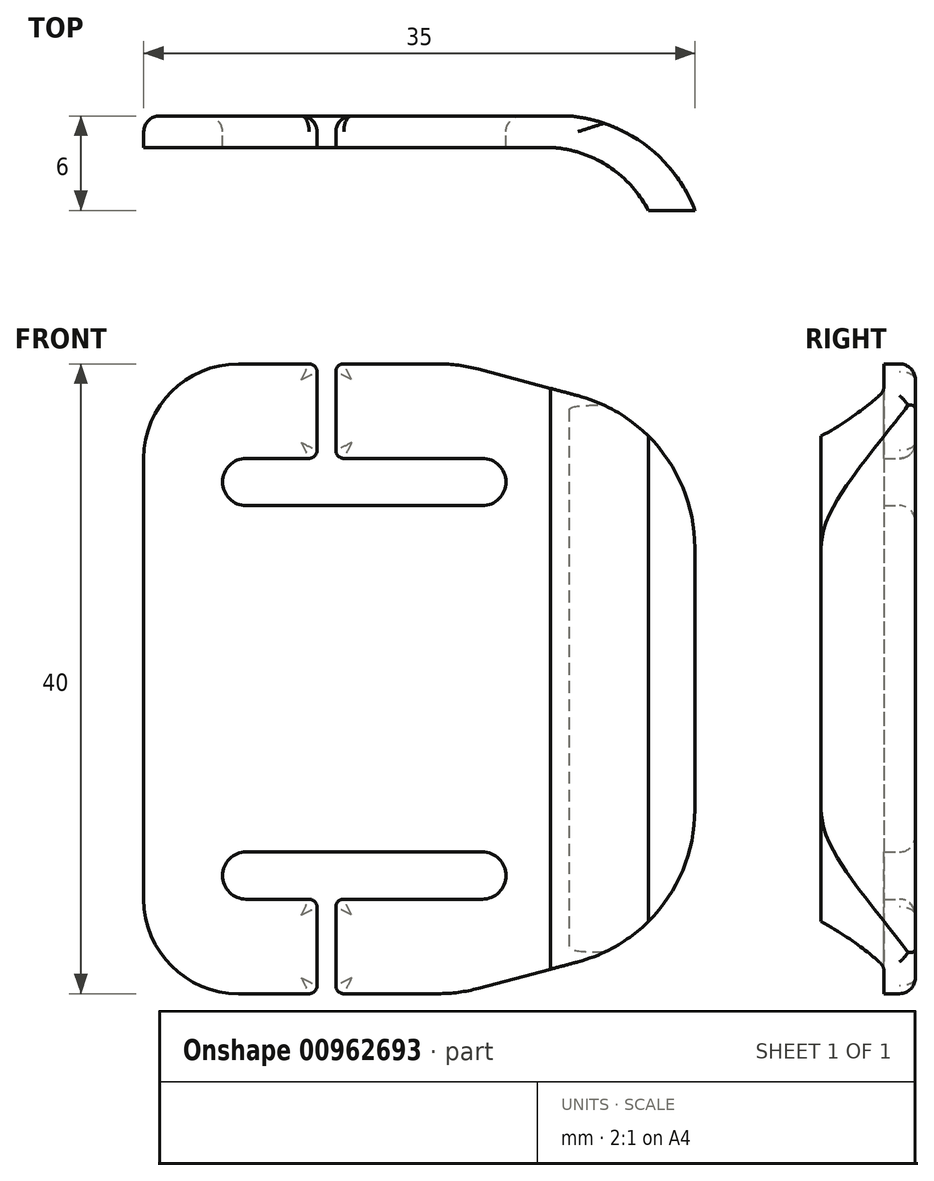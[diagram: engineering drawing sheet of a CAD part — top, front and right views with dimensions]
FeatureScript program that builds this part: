
annotation { "Feature Type Name" : "Feature", "Feature Type Description" : "" }
export const myFeature = defineFeature(function(context is Context, id is Id, definition is map)
    precondition{}
    {
        {
            var Q0;
            Q0=qCreatedBy(makeId("Front.planeOp"),FACE);
            var sketch = newSketch(context, id + "F0", { "sketchPlane" : qUnion([Q0])});
            skLineSegment(sketch, "E0.bottom", {"start": v(1, -20) * mm, "end": v(5.5, -20) * mm});
            skLineSegment(sketch, "E0.top", {"start": v(1, 20) * mm, "end": v(5.5, 20) * mm});
            skLineSegment(sketch, "E0.left", {"start": v(-5, -14) * mm, "end": v(-5, 14) * mm});
            skLineSegment(sketch, "E0.right", {"start": v(30, -8.32) * mm, "end": v(30, 8.32) * mm});
            skLineSegment(sketch, "E1.bottom", {"start": v(1.5, 14) * mm, "end": v(5.5, 14) * mm});
            skLineSegment(sketch, "E1.top", {"start": v(1.5, 11) * mm, "end": v(16.5, 11) * mm});
            skLineSegment(sketch, "E1.left", {"start": v(0, 12.5) * mm, "end": v(0, 12.5) * mm});
            skLineSegment(sketch, "E1.right", {"start": v(18, 12.5) * mm, "end": v(18, 12.5) * mm});
            skLineSegment(sketch, "E2.bottom", {"start": v(1.5, -11) * mm, "end": v(16.5, -11) * mm});
            skLineSegment(sketch, "E2.top", {"start": v(1.5, -14) * mm, "end": v(5.5, -14) * mm});
            skLineSegment(sketch, "E2.left", {"start": v(0, -12.5) * mm, "end": v(0, -12.5) * mm});
            skLineSegment(sketch, "E2.right", {"start": v(18, -12.5) * mm, "end": v(18, -12.5) * mm});
            skPoint(sketch, "E3.visualSharp", {"position": v(-5, 20) * mm});
            skArc(sketch, "E3.filletArc", {"start": v(1, 20) * mm, "mid": v(-3.24, 18.24) * mm, "end": v(-5, 14) * mm});
            skPoint(sketch, "E4.visualSharp", {"position": v(-5, -20) * mm});
            skArc(sketch, "E4.filletArc", {"start": v(-5, -14) * mm, "mid": v(-3.24, -18.24) * mm, "end": v(1, -20) * mm});
            skLineSegment(sketch, "E5", {"start": v(6, 19.5) * mm, "end": v(6, 14.5) * mm});
            skLineSegment(sketch, "E6", {"start": v(7.2, 19.5) * mm, "end": v(7.2, 14.5) * mm});
            skLineSegment(sketch, "E7.trimOffspring", {"start": v(6, -14.5) * mm, "end": v(6, -19.5) * mm});
            skLineSegment(sketch, "E8.trimOffspring", {"start": v(7.2, -14.5) * mm, "end": v(7.2, -19.5) * mm});
            skLineSegment(sketch, "E9.trimOffspring", {"start": v(7.7, -20) * mm, "end": v(13.69, -20) * mm});
            skLineSegment(sketch, "E10.trimOffspring", {"start": v(7.7, -14) * mm, "end": v(16.5, -14) * mm});
            skLineSegment(sketch, "E11.trimOffspring", {"start": v(7.7, 14) * mm, "end": v(16.5, 14) * mm});
            skLineSegment(sketch, "E12.trimOffspring", {"start": v(7.7, 20) * mm, "end": v(13.69, 20) * mm});
            skPoint(sketch, "E13.visualSharp", {"position": v(0, 14) * mm});
            skArc(sketch, "E13.filletArc", {"start": v(1.5, 14) * mm, "mid": v(0.44, 13.56) * mm, "end": v(0, 12.5) * mm});
            skPoint(sketch, "E14.visualSharp", {"position": v(0, 11) * mm});
            skArc(sketch, "E14.filletArc", {"start": v(0, 12.5) * mm, "mid": v(0.44, 11.44) * mm, "end": v(1.5, 11) * mm});
            skPoint(sketch, "E15.visualSharp", {"position": v(18, 14) * mm});
            skArc(sketch, "E15.filletArc", {"start": v(18, 12.5) * mm, "mid": v(17.56, 13.56) * mm, "end": v(16.5, 14) * mm});
            skPoint(sketch, "E16.visualSharp", {"position": v(18, 11) * mm});
            skArc(sketch, "E16.filletArc", {"start": v(16.5, 11) * mm, "mid": v(17.56, 11.44) * mm, "end": v(18, 12.5) * mm});
            skPoint(sketch, "E17.visualSharp", {"position": v(0, -11) * mm});
            skArc(sketch, "E17.filletArc", {"start": v(1.5, -11) * mm, "mid": v(0.44, -11.44) * mm, "end": v(0, -12.5) * mm});
            skPoint(sketch, "E18.visualSharp", {"position": v(0, -14) * mm});
            skArc(sketch, "E18.filletArc", {"start": v(0, -12.5) * mm, "mid": v(0.44, -13.56) * mm, "end": v(1.5, -14) * mm});
            skPoint(sketch, "E19.visualSharp", {"position": v(18, -11) * mm});
            skArc(sketch, "E19.filletArc", {"start": v(18, -12.5) * mm, "mid": v(17.56, -11.44) * mm, "end": v(16.5, -11) * mm});
            skPoint(sketch, "E20.visualSharp", {"position": v(18, -14) * mm});
            skArc(sketch, "E20.filletArc", {"start": v(16.5, -14) * mm, "mid": v(17.56, -13.56) * mm, "end": v(18, -12.5) * mm});
            skPoint(sketch, "E21.visualSharp", {"position": v(6, 14) * mm});
            skArc(sketch, "E21.filletArc", {"start": v(5.5, 14) * mm, "mid": v(5.85, 14.15) * mm, "end": v(6, 14.5) * mm});
            skPoint(sketch, "E22.visualSharp", {"position": v(7.2, 14) * mm});
            skArc(sketch, "E22.filletArc", {"start": v(7.2, 14.5) * mm, "mid": v(7.35, 14.15) * mm, "end": v(7.7, 14) * mm});
            skPoint(sketch, "E23.visualSharp", {"position": v(6, 20) * mm});
            skArc(sketch, "E23.filletArc", {"start": v(6, 19.5) * mm, "mid": v(5.85, 19.85) * mm, "end": v(5.5, 20) * mm});
            skPoint(sketch, "E24.visualSharp", {"position": v(7.2, 20) * mm});
            skArc(sketch, "E24.filletArc", {"start": v(7.7, 20) * mm, "mid": v(7.35, 19.85) * mm, "end": v(7.2, 19.5) * mm});
            skPoint(sketch, "E25.visualSharp", {"position": v(6, -20) * mm});
            skArc(sketch, "E25.filletArc", {"start": v(5.5, -20) * mm, "mid": v(5.85, -19.85) * mm, "end": v(6, -19.5) * mm});
            skPoint(sketch, "E26.visualSharp", {"position": v(7.2, -20) * mm});
            skArc(sketch, "E26.filletArc", {"start": v(7.2, -19.5) * mm, "mid": v(7.35, -19.85) * mm, "end": v(7.7, -20) * mm});
            skPoint(sketch, "E27.visualSharp", {"position": v(6, -14) * mm});
            skArc(sketch, "E27.filletArc", {"start": v(6, -14.5) * mm, "mid": v(5.85, -14.15) * mm, "end": v(5.5, -14) * mm});
            skPoint(sketch, "E28.visualSharp", {"position": v(7.2, -14) * mm});
            skArc(sketch, "E28.filletArc", {"start": v(7.7, -14) * mm, "mid": v(7.35, -14.15) * mm, "end": v(7.2, -14.5) * mm});
            skLineSegment(sketch, "E29", {"start": v(16.27, -19.66) * mm, "end": v(22.58, -17.98) * mm});
            skPoint(sketch, "E30.visualSharp", {"position": v(15, -20) * mm});
            skArc(sketch, "E30.filletArc", {"start": v(13.69, -20) * mm, "mid": v(14.99, -19.92) * mm, "end": v(16.27, -19.66) * mm});
            skPoint(sketch, "E31.visualSharp", {"position": v(30, -16) * mm});
            skArc(sketch, "E31.filletArc", {"start": v(22.58, -17.98) * mm, "mid": v(27.93, -14.4) * mm, "end": v(30, -8.32) * mm});
            skArc(sketch, "E32.MirrorCS", {"start": v(22.58, 17.98) * mm, "mid": v(27.93, 14.4) * mm, "end": v(30, 8.32) * mm});
            skLineSegment(sketch, "E33.MirrorCS", {"start": v(16.27, 19.66) * mm, "end": v(22.58, 17.98) * mm});
            skArc(sketch, "E34.MirrorCS", {"start": v(13.69, 20) * mm, "mid": v(14.99, 19.92) * mm, "end": v(16.27, 19.66) * mm});
            skSolve(sketch);
        }
        {
            var Q0;
            Q0 = qSketchRegion(id + "F0", true);
            extrude(context, id + "F1", {"entities" : qUnion([Q0]), "depth" : 6 * mm, "offsetDistance" : 25 * mm});
        }
        {
            var Q0;
            Q0=makeQuery(id+"F1.opExtrude","SWEPT_FACE",FACE,{"disambiguationData":[OSD([sQuery(id+"F0.wireOp",EDGE,"E9.trimOffspring")])]});
            var sketch = newSketch(context, id + "F2", { "sketchPlane" : qUnion([Q0])});
            skLineSegment(sketch, "E35", {"start": v(-6.5, 2) * mm, "end": v(20.84, 2) * mm});
            skArc(sketch, "E36", {"start": v(20.84, 2) * mm, "mid": v(24.47, 3.17) * mm, "end": v(27.04, 6) * mm});
            skArc(sketch, "E37", {"start": v(22, 0) * mm, "mid": v(26.87, 1.85) * mm, "end": v(30, 6) * mm});
            skLineSegment(sketch, "E38", {"start": v(-7.66, 0) * mm, "end": v(22, 0) * mm});
            skPoint(sketch, "E39.orphan", {"position": v(30.17, 6) * mm});
            skPoint(sketch, "E40.orphan", {"position": v(-7.66, 0) * mm});
            skLineSegment(sketch, "E41", {"start": v(-6.5, 2) * mm, "end": v(-6.5, 8.41) * mm});
            skLineSegment(sketch, "E42", {"start": v(-6.5, 8.41) * mm, "end": v(27.04, 8.41) * mm});
            skLineSegment(sketch, "E43", {"start": v(27.04, 8.41) * mm, "end": v(27.04, 6) * mm});
            skLineSegment(sketch, "E44", {"start": v(-7.66, 0) * mm, "end": v(-7.66, -2.54) * mm});
            skLineSegment(sketch, "E45", {"start": v(-7.66, -2.54) * mm, "end": v(31.35, -2.54) * mm});
            skLineSegment(sketch, "E46", {"start": v(31.35, -2.54) * mm, "end": v(31.35, 6) * mm});
            skLineSegment(sketch, "E47", {"start": v(31.35, 6) * mm, "end": v(30, 6) * mm});
            skSolve(sketch);
        }
        {
            var Q0;
            {var subQ3=sQuery(id+"F2.wireOp",EDGE,"E37");Q0=makeQuery(id+"F2.imprint","IMPRINT",FACE,{"disambiguationData":[TD([[makeQuery(id+"F2.imprint","IMPRINT",EDGE,{"derivedFrom":subQ3}),-1.0]])]});}
            var Q1;
            {var subQ6=sQuery(id+"F2.wireOp",EDGE,"E36");Q1=makeQuery(id+"F2.imprint","IMPRINT",FACE,{"disambiguationData":[TD([[makeQuery(id+"F2.imprint","IMPRINT",EDGE,{"derivedFrom":subQ6}),1.0]])]});}
            var Q2;
            {var subQ1=sQuery(id+"F0.wireOp",EDGE,"E9.trimOffspring");var subQ6=makeQuery(id+"F1.opExtrude","CAP_EDGE",EDGE,{"disambiguationData":[OSD([subQ1])],"isStart":false});Q2=makeQuery(id+"F2.imprint","IMPRINT",FACE,{"disambiguationData":[TD([[makeQuery(id+"F2.imprint","IMPRINT",EDGE,{"derivedFrom":subQ6}),-1.0]])]});}
            var Q3;
            Q3=sQuery(id+"F2.wireOp",EDGE,"E38");
            extrude(context, id + "F3", {"entities" : qUnion([Q0, Q1, Q2]), "operationType" : NewBodyOperationType.REMOVE, "surfaceEntities" : qUnion([Q3]), "endBound" : BoundingType.THROUGH_ALL, "oppositeDirection" : true, "depth" : 100 * mm, "offsetDistance" : 25 * mm});
        }
        {
            var Q0;
            Q0=makeQuery(id+"F1.opExtrude","CAP_EDGE",EDGE,{"disambiguationData":[OSD([sQuery(id+"F0.wireOp",EDGE,"E0.left")])],"isStart":true});
            fillet(context, id + "F4", {"entities" : qUnion([Q0]), "radius" : 1 * mm, "tangentPropagation" : true, "allowEdgeOverflow" : false});
        }
    });
